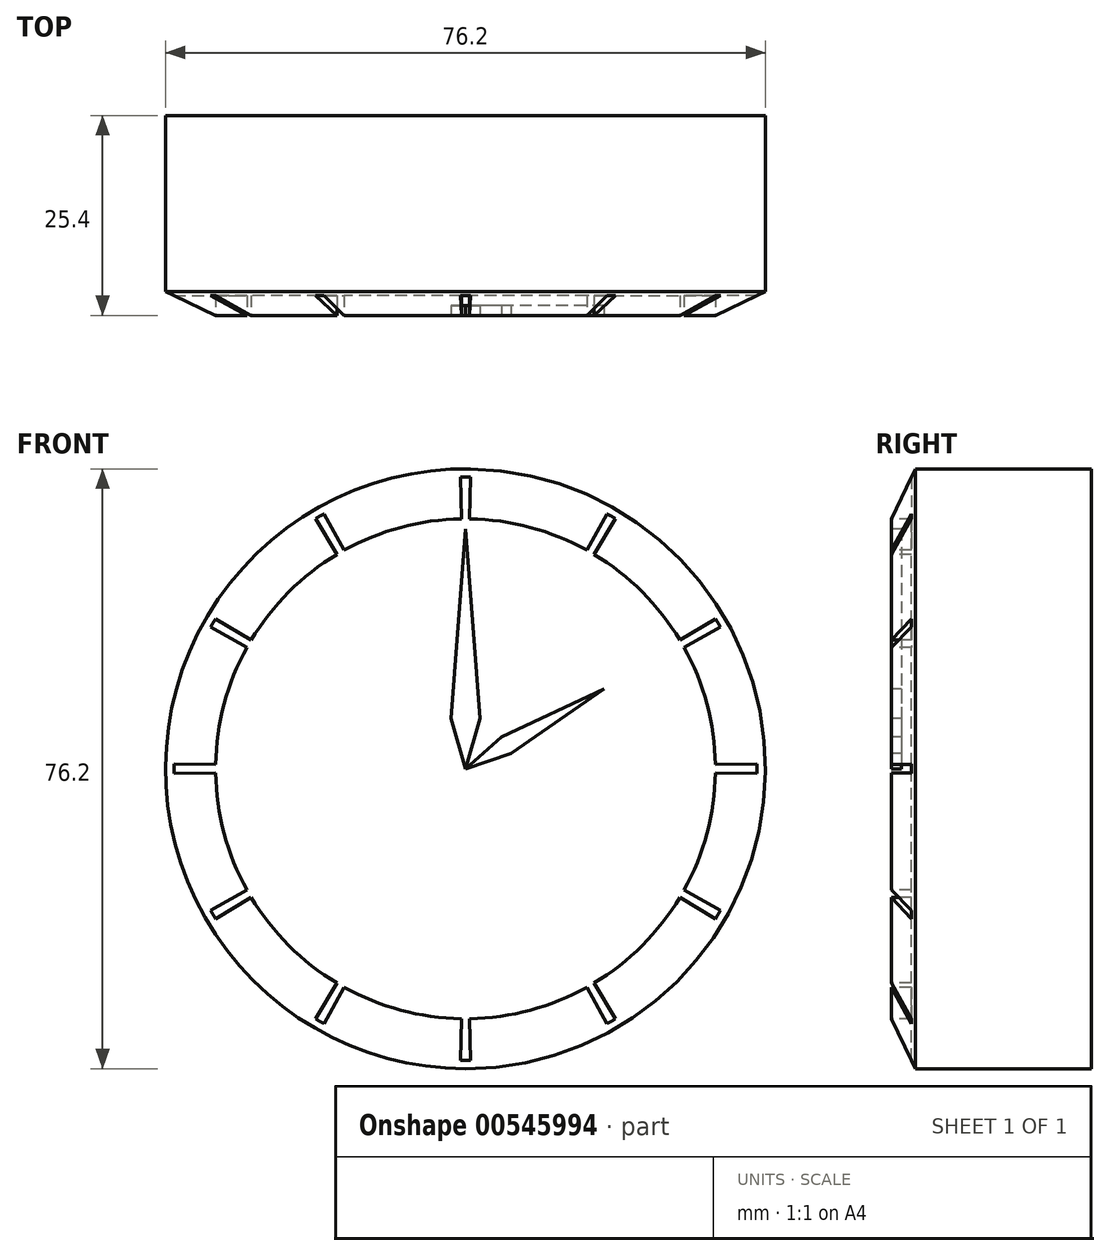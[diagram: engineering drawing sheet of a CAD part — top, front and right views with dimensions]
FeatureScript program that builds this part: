
annotation { "Feature Type Name" : "Feature", "Feature Type Description" : "" }
export const myFeature = defineFeature(function(context is Context, id is Id, definition is map)
    precondition{}
    {
        {
            var Q0;
            Q0=qCreatedBy(makeId("Front.planeOp"),FACE);
            var sketch = newSketch(context, id + "F0", { "sketchPlane" : qUnion([Q0])});
            skCircle(sketch, "E0", {"center": v(0, 0) * mm, "radius": 38.1 * mm});
            skSolve(sketch);
        }
        {
            var Q0;
            Q0 = qSketchRegion(id + "F0", true);
            extrude(context, id + "F1", {"entities" : qUnion([Q0]), "depth" : 25.4 * mm, "offsetDistance" : 25.4 * mm});
        }
        {
            var Q0;
            Q0=makeQuery(id+"F1.opExtrude","CAP_FACE",FACE,{"disambiguationData":[OSD([sQuery(id+"F0.wireOp",EDGE,"E0")])],"isStart":false});
            var sketch = newSketch(context, id + "F2", { "sketchPlane" : qUnion([Q0])});
            skCircle(sketch, "E1", {"center": v(0, 0) * mm, "radius": 31.75 * mm});
            skArc(sketch, "E2", {"start": v(-0.63, 38.1) * mm, "mid": v(0, 38.1) * mm, "end": v(0.63, 38.1) * mm});
            skLineSegment(sketch, "E3", {"start": v(0, 38.1) * mm, "end": v(0, 0) * mm, "construction": true});
            skLineSegment(sketch, "E4", {"start": v(-0.63, 38.1) * mm, "end": v(0, 0) * mm, "construction": true});
            skLineSegment(sketch, "E5", {"start": v(0.63, 38.1) * mm, "end": v(0, 0) * mm, "construction": true});
            skLineSegment(sketch, "E6", {"start": v(-0.63, 38.1) * mm, "end": v(-0.53, 31.75) * mm});
            skLineSegment(sketch, "E7", {"start": v(0.63, 38.1) * mm, "end": v(0.53, 31.75) * mm});
            skLineSegment(sketch, "E8.1.0", {"start": v(-18.5, 33.3) * mm, "end": v(0, 0) * mm, "construction": true});
            skLineSegment(sketch, "E8.1.1", {"start": v(-19.6, 32.67) * mm, "end": v(0, 0) * mm, "construction": true});
            skLineSegment(sketch, "E8.1.2", {"start": v(-19.05, 33) * mm, "end": v(0, 0) * mm, "construction": true});
            skLineSegment(sketch, "E8.1.3", {"start": v(-18.5, 33.3) * mm, "end": v(-15.41, 27.76) * mm});
            skLineSegment(sketch, "E8.1.4", {"start": v(-19.6, 32.67) * mm, "end": v(-16.33, 27.23) * mm});
            skArc(sketch, "E8.1.5", {"start": v(-19.6, 32.67) * mm, "mid": v(-19.05, 33) * mm, "end": v(-18.5, 33.3) * mm});
            skLineSegment(sketch, "E8.2.0", {"start": v(-32.67, 19.6) * mm, "end": v(0, 0) * mm, "construction": true});
            skLineSegment(sketch, "E8.2.1", {"start": v(-33.3, 18.5) * mm, "end": v(0, 0) * mm, "construction": true});
            skLineSegment(sketch, "E8.2.2", {"start": v(-33, 19.05) * mm, "end": v(0, 0) * mm, "construction": true});
            skLineSegment(sketch, "E8.2.3", {"start": v(-32.67, 19.6) * mm, "end": v(-27.23, 16.33) * mm});
            skLineSegment(sketch, "E8.2.4", {"start": v(-33.3, 18.5) * mm, "end": v(-27.76, 15.41) * mm});
            skArc(sketch, "E8.2.5", {"start": v(-33.3, 18.5) * mm, "mid": v(-33, 19.05) * mm, "end": v(-32.67, 19.6) * mm});
            skLineSegment(sketch, "E8.3.0", {"start": v(-38.1, 0.63) * mm, "end": v(0, 0) * mm, "construction": true});
            skLineSegment(sketch, "E8.3.1", {"start": v(-38.1, -0.63) * mm, "end": v(0, 0) * mm, "construction": true});
            skLineSegment(sketch, "E8.3.2", {"start": v(-38.1, 0) * mm, "end": v(0, 0) * mm, "construction": true});
            skLineSegment(sketch, "E8.3.3", {"start": v(-38.1, 0.63) * mm, "end": v(-31.75, 0.53) * mm});
            skLineSegment(sketch, "E8.3.4", {"start": v(-38.1, -0.63) * mm, "end": v(-31.75, -0.53) * mm});
            skArc(sketch, "E8.3.5", {"start": v(-38.1, -0.63) * mm, "mid": v(-38.1, 0) * mm, "end": v(-38.1, 0.63) * mm});
            skLineSegment(sketch, "E8.4.0", {"start": v(-33.3, -18.5) * mm, "end": v(0, 0) * mm, "construction": true});
            skLineSegment(sketch, "E8.4.1", {"start": v(-32.67, -19.6) * mm, "end": v(0, 0) * mm, "construction": true});
            skLineSegment(sketch, "E8.4.2", {"start": v(-33, -19.05) * mm, "end": v(0, 0) * mm, "construction": true});
            skLineSegment(sketch, "E8.4.3", {"start": v(-33.3, -18.5) * mm, "end": v(-27.76, -15.41) * mm});
            skLineSegment(sketch, "E8.4.4", {"start": v(-32.67, -19.6) * mm, "end": v(-27.23, -16.33) * mm});
            skArc(sketch, "E8.4.5", {"start": v(-32.67, -19.6) * mm, "mid": v(-33, -19.05) * mm, "end": v(-33.3, -18.5) * mm});
            skLineSegment(sketch, "E8.5.0", {"start": v(-19.6, -32.67) * mm, "end": v(0, 0) * mm, "construction": true});
            skLineSegment(sketch, "E8.5.1", {"start": v(-18.5, -33.3) * mm, "end": v(0, 0) * mm, "construction": true});
            skLineSegment(sketch, "E8.5.2", {"start": v(-19.05, -33) * mm, "end": v(0, 0) * mm, "construction": true});
            skLineSegment(sketch, "E8.5.3", {"start": v(-19.6, -32.67) * mm, "end": v(-16.33, -27.23) * mm});
            skLineSegment(sketch, "E8.5.4", {"start": v(-18.5, -33.3) * mm, "end": v(-15.41, -27.76) * mm});
            skArc(sketch, "E8.5.5", {"start": v(-18.5, -33.3) * mm, "mid": v(-19.05, -33) * mm, "end": v(-19.6, -32.67) * mm});
            skLineSegment(sketch, "E8.6.0", {"start": v(-0.63, -38.1) * mm, "end": v(0, 0) * mm, "construction": true});
            skLineSegment(sketch, "E8.6.1", {"start": v(0.63, -38.1) * mm, "end": v(0, 0) * mm, "construction": true});
            skLineSegment(sketch, "E8.6.2", {"start": v(0, -38.1) * mm, "end": v(0, 0) * mm, "construction": true});
            skLineSegment(sketch, "E8.6.3", {"start": v(-0.63, -38.1) * mm, "end": v(-0.53, -31.75) * mm});
            skLineSegment(sketch, "E8.6.4", {"start": v(0.63, -38.1) * mm, "end": v(0.53, -31.75) * mm});
            skArc(sketch, "E8.6.5", {"start": v(0.63, -38.1) * mm, "mid": v(0, -38.1) * mm, "end": v(-0.63, -38.1) * mm});
            skLineSegment(sketch, "E8.7.0", {"start": v(18.5, -33.3) * mm, "end": v(0, 0) * mm, "construction": true});
            skLineSegment(sketch, "E8.7.1", {"start": v(19.6, -32.67) * mm, "end": v(0, 0) * mm, "construction": true});
            skLineSegment(sketch, "E8.7.2", {"start": v(19.05, -33) * mm, "end": v(0, 0) * mm, "construction": true});
            skLineSegment(sketch, "E8.7.3", {"start": v(18.5, -33.3) * mm, "end": v(15.41, -27.76) * mm});
            skLineSegment(sketch, "E8.7.4", {"start": v(19.6, -32.67) * mm, "end": v(16.33, -27.23) * mm});
            skArc(sketch, "E8.7.5", {"start": v(19.6, -32.67) * mm, "mid": v(19.05, -33) * mm, "end": v(18.5, -33.3) * mm});
            skLineSegment(sketch, "E8.8.0", {"start": v(32.67, -19.6) * mm, "end": v(0, 0) * mm, "construction": true});
            skLineSegment(sketch, "E8.8.1", {"start": v(33.3, -18.5) * mm, "end": v(0, 0) * mm, "construction": true});
            skLineSegment(sketch, "E8.8.2", {"start": v(33, -19.05) * mm, "end": v(0, 0) * mm, "construction": true});
            skLineSegment(sketch, "E8.8.3", {"start": v(32.67, -19.6) * mm, "end": v(27.23, -16.33) * mm});
            skLineSegment(sketch, "E8.8.4", {"start": v(33.3, -18.5) * mm, "end": v(27.76, -15.41) * mm});
            skArc(sketch, "E8.8.5", {"start": v(33.3, -18.5) * mm, "mid": v(33, -19.05) * mm, "end": v(32.67, -19.6) * mm});
            skLineSegment(sketch, "E8.9.0", {"start": v(38.1, -0.63) * mm, "end": v(0, 0) * mm, "construction": true});
            skLineSegment(sketch, "E8.9.1", {"start": v(38.1, 0.63) * mm, "end": v(0, 0) * mm, "construction": true});
            skLineSegment(sketch, "E8.9.2", {"start": v(38.1, 0) * mm, "end": v(0, 0) * mm, "construction": true});
            skLineSegment(sketch, "E8.9.3", {"start": v(38.1, -0.63) * mm, "end": v(31.75, -0.53) * mm});
            skLineSegment(sketch, "E8.9.4", {"start": v(38.1, 0.63) * mm, "end": v(31.75, 0.53) * mm});
            skArc(sketch, "E8.9.5", {"start": v(38.1, 0.63) * mm, "mid": v(38.1, 0) * mm, "end": v(38.1, -0.63) * mm});
            skLineSegment(sketch, "E8.10.0", {"start": v(33.3, 18.5) * mm, "end": v(0, 0) * mm, "construction": true});
            skLineSegment(sketch, "E8.10.1", {"start": v(32.67, 19.6) * mm, "end": v(0, 0) * mm, "construction": true});
            skLineSegment(sketch, "E8.10.2", {"start": v(33, 19.05) * mm, "end": v(0, 0) * mm, "construction": true});
            skLineSegment(sketch, "E8.10.3", {"start": v(33.3, 18.5) * mm, "end": v(27.76, 15.41) * mm});
            skLineSegment(sketch, "E8.10.4", {"start": v(32.67, 19.6) * mm, "end": v(27.23, 16.33) * mm});
            skArc(sketch, "E8.10.5", {"start": v(32.67, 19.6) * mm, "mid": v(33, 19.05) * mm, "end": v(33.3, 18.5) * mm});
            skLineSegment(sketch, "E8.11.0", {"start": v(19.6, 32.67) * mm, "end": v(0, 0) * mm, "construction": true});
            skLineSegment(sketch, "E8.11.1", {"start": v(18.5, 33.3) * mm, "end": v(0, 0) * mm, "construction": true});
            skLineSegment(sketch, "E8.11.2", {"start": v(19.05, 33) * mm, "end": v(0, 0) * mm, "construction": true});
            skLineSegment(sketch, "E8.11.3", {"start": v(19.6, 32.67) * mm, "end": v(16.33, 27.23) * mm});
            skLineSegment(sketch, "E8.11.4", {"start": v(18.5, 33.3) * mm, "end": v(15.41, 27.76) * mm});
            skArc(sketch, "E8.11.5", {"start": v(18.5, 33.3) * mm, "mid": v(19.05, 33) * mm, "end": v(19.6, 32.67) * mm});
            skSolve(sketch);
        }
        {
            var Q0;
            Q0=makeQuery(id+"F1.opExtrude","CAP_FACE",FACE,{"disambiguationData":[OSD([sQuery(id+"F0.wireOp",EDGE,"E0")])],"isStart":false});
            chamfer(context, id + "F3", {"entities" : qUnion([Q0]), "chamferType" : ChamferType.TWO_OFFSETS, "width1" : 6.35 * mm, "oppositeDirection" : false, "width2" : 3.05 * mm, "tangentPropagation" : true});
        }
        {
            var Q0;
            Q0 = qSketchRegion(id + "F2", true);
            extrude(context, id + "F4", {"entities" : qUnion([Q0]), "operationType" : NewBodyOperationType.REMOVE, "oppositeDirection" : true, "depth" : 2.54 * mm, "offsetDistance" : 25.4 * mm});
        }
        {
            var Q0;
            {var subQ0=sQuery(id+"F2.wireOp",EDGE,"E1");var subQ8=makeQuery(id+"F2.imprint","INTERSECT",VERTEX,{"derivedFrom":[subQ0,sQuery(id+"F2.wireOp",EDGE,"00b4139b-6b62-422e-b0bf-90bcdbad7413.9.0")]});Q0=makeQuery(id+"F2.imprint","IMPRINT",FACE,{"disambiguationData":[TD([[makeQuery(id+"F2.imprint","IMPRINT",EDGE,{"disambiguationData":[TD([[subQ8,-1.0]])],"derivedFrom":subQ0}),1.0]])]});}
            var sketch = newSketch(context, id + "F5", { "sketchPlane" : qUnion([Q0])});
            skLineSegment(sketch, "E9", {"start": v(0, 0) * mm, "end": v(0, 30.48) * mm, "construction": true});
            skLineSegment(sketch, "E10", {"start": v(0, 0) * mm, "end": v(17.6, 10.16) * mm, "construction": true});
            skLineSegment(sketch, "E11", {"start": v(0, 30.48) * mm, "end": v(-1.84, 6.41) * mm});
            skLineSegment(sketch, "E12", {"start": v(-1.84, 6.41) * mm, "end": v(0, 0) * mm});
            skLineSegment(sketch, "E13", {"start": v(17.6, 10.16) * mm, "end": v(4.58, 4.06) * mm});
            skLineSegment(sketch, "E14", {"start": v(4.58, 4.06) * mm, "end": v(0, 0) * mm});
            skLineSegment(sketch, "E15.MirrorCS", {"start": v(0, 30.48) * mm, "end": v(1.84, 6.41) * mm});
            skLineSegment(sketch, "E16.MirrorCS", {"start": v(1.84, 6.41) * mm, "end": v(0, 0) * mm});
            skLineSegment(sketch, "E17.MirrorCS", {"start": v(17.6, 10.16) * mm, "end": v(5.8, 1.94) * mm});
            skLineSegment(sketch, "E18.MirrorCS", {"start": v(5.8, 1.94) * mm, "end": v(0, 0) * mm});
            skSolve(sketch);
        }
        {
            var Q0;
            Q0 = qSketchRegion(id + "F5", true);
            extrude(context, id + "F6", {"entities" : qUnion([Q0]), "operationType" : NewBodyOperationType.ADD, "oppositeDirection" : true, "depth" : 1.27 * mm, "offsetDistance" : 25.4 * mm});
        }
    });
